# Revit family: PRE050012-FR
name_source: partatom
category: Accessoire de canalisation
revit_build: Autodesk Revit 2017 (Build: 20160225_1515(x64)
units: mm (PartAtom-declared; Revit-internal decimal feet)

## family parameters
Basée sur le plan de construction = Non
Cote de connecteur circulaire = Utiliser le diamètre
Couper avec des vides une fois chargée = Non
Partagée = Non
Toujours verticalement = Oui
Type d'élément = Normal

## types (5) — shared parameters
Adresse = 7, RUE RACINE - 92542 MONTROUGE CEDEX FRANCE
Diamètre Nominal = 12 mm  [stored 0.0393701 ft]
Fabricant = LES ROBINETS PRESTO S.A.
Finition = Composants en métal injecté avec traitement nickel-chrome

Corps en métal moulé injecté
Garantie = 3
Hauteur = 150 mm  [stored 0.492126 ft]
LC = 28 mm  [stored 0.0918635 ft]
Largeur = 56 mm  [stored 0.183727 ft]
Lien CCTP = http://www.prestodatashare.com
Lien fiche produit = http://www.prestodatashare.com
Lien notice d'utilisation = http://www.prestodatashare.com
Matériau = Laiton poli chromé
PC = 30 mm  [stored 0.0984252 ft]
Perte de charge = 0.0 Pa
Pression = 1 à 5 bars
Profondeur = 168 mm  [stored 0.551181 ft]
Raccordement = G 3/8" (12x17) en eau froide, chaude ou pré-mitigée
URL = http://www.prestodatashare.com
URL Fabricant = http://www.prestodatashare.com
Variantes = 56632-56633-56634-55635-56654

## per-type parameters (varying)
| type | Debit | Description | Flux | Fonction | Polantis code | Reference |
| 56632 PRESTO TOUCH SIMPLE PILE SS RA | 3 l/min par limiteur de débit intégré

Aérateur anti-tartre haute qualité

Dispositif anti-coup de bélier | Robinet simple sensitif (CE) temporisé (1s à 5mn) sur plage, alimentation en  eau froide ou mitigée. De type Presto TOUCH® réf. 56633 ou techniquement équivalent. Avec fonction start /stop par effleurement et régulateur de débit intégré (3 l/min). Alimentation par pile lithium 6 V intégrée dans le robinet. Avec flexibles PEX et filtre panier. Purge automatique paramétrable. | 0.1 L/s | Pression d'utilisation recommandée :
- 1 à 5 bars

Débit :
- 3 l/min par limiteur de débit intégré
- Aérateur anti-tartre haute qualité
- Dispositif anti-coup de bélier

Durée d'écoulement :
- 6 secondes (Réglable de 1 s à 5 min) et fonction marche/arrêt
- Fréquence et durée d'écoulement forcé paramétrables

Alimentation hydraulique:
- G 3/8" (12x17) en eau froide, chaude ou pré-mitigée

Alimentation électrique :
- Modèle avec pile lithium 6 volts type CRP2

Matière et couleur de finition :
- Composants en métal injecté avec traitement nickel-chrome
- Corps en métal moulé injecté

Résistance thermique :
- Ce robinet résiste à une température de 75°C durant 30 minutes dans le cadre de chocs thermiques

Sécurité :
- Fermeture automatique de l'électrovanne en cas d'usure de la pile

Livré avec :
- 1 Flexible PEX avec écrou femelle 3/8'' (12x17) et clapet anti-retour NF
- 1 Joint filtre monté dans une douille laiton
- 1 Bride de fixation
- 1 Joint de bride
- 1 Ecrou de fixation
- 1 Notice de pose

Normes / Agréments :
- Traitement de surface Nickel-chrome selon NF EN12540
- Résistance au brouillard salin neutre (NSS) : 200 h selon NF ISO 9227 | PRE050012-FR | 56632 |
| 56654 PRESTO TOUCH SIMPLE PILE RA - DEBIT 2L/MIN | 1,9 l/min par limiteur de débit intégré
 (sprayer)
 Aérateur anti-tartre haute qualité

 Dispositif anti-coup de bélier | Robinet simple sensitif (CE) temporisé (1s à 5mn) sur plage, alimentation en  eau froide ou mitigée. De type Presto TOUCH® réf. 56654 ou techniquement équivalent. Avec fonction start /stop par effleurement et limiteur de débit intégré (1,9 l/mn). Alimentation par pile lithium 6 V intégrée dans le robinet. Avec flexibles PEX, robinet d’arrêt droit et filtre panier. Purge automatique paramétrable. | 0.0 L/s | Pression d'utilisation recommandée :
- 1 à 5 bars

Débit :
- 1,9 l/min par sprayer limiteur de débit intégré
- Aérateur anti-tartre haute qualité
- Dispositif anti-coup de bélier

Durée d'écoulement :
- 6 secondes (Réglable de 1 s à 5 min) et fonction marche/arrêt
- Fréquence et durée d'écoulement forcé paramétrables

Alimentation hydraulique:
- G 3/8" (12x17) en eau froide, chaude ou pré-mitigée

Alimentation électrique :
- Modèle avec pile lithium 6 volts type CRP2

Matière et couleur de finition :
- Composants en métal injecté avec traitement nickel-chrome
- Corps en métal moulé injecté

Résistance thermique :
- Ce robinet résiste à une température de 75°C durant 30 minutes dans le cadre de chocs thermiques

Sécurité :
- Fermeture automatique de l'électrovanne en cas d'usure de la pile

Livré avec :
- 1 Flexible PEX avec écrou femelle 3/8'' (12x17) et clapet anti-retour NF
- 1 Joint filtre monté dans une douille laiton
- 1 Robinet d'arrêt droit G 3/8'' (12x17)
- 1 Bride de fixation
- 1 Joint de bride
- 1 Ecrou de fixation
- 1 Notice de pose

Normes / Agréments :
- Traitement de surface Nickel-chrome selon NF EN12540
- Résistance au brouillard salin neutre (NSS) : 200 h selon NF ISO 9227 | PRE050012d-FR | 56654 |
| 56635 PRESTO TOUCH SIMPLE SECTEUR RA | 3 l/min par limiteur de débit intégré

Aérateur anti-tartre haute qualité

Dispositif anti-coup de bélier | Robinet simple sensitif (CE) temporisé (1s à 5mn) sur plage, alimentation en  eau froide ou mitigée. De type Presto TOUCH® réf. 56635 ou techniquement équivalent. Avec fonction start /stop par effleurement et régulateur de débit intégré (3 l/min). Alimentation secteur par transformateur 230/7 Volt déporté dans boîtier étanche IP65. Avec flexible PEX, robinet d’arrêt droit et filtre panier. Purge automatique paramétrable. | 0.1 L/s | Pression d'utilisation recommandée :
- 1 à 5 bars

Débit :
- 3 l/min par limiteur de débit intégré
- Aérateur anti-tartre haute qualité
- Dispositif anti-coup de bélier

Durée d'écoulement :
- 6 secondes (Réglable de 1 s à 5 min) et fonction marche/arrêt
- Fréquence et durée d'écoulement forcé paramétrables

Alimentation hydraulique:
- G 3/8" (12x17) en eau froide, chaude ou pré-mitigée

Alimentation électrique :
- Avec transformateur 230 VAC / 7 VDC dans boîtier étanche IP65

Matière et couleur de finition :
- Composants en métal injecté avec traitement nickel-chrome
- Corps en métal moulé injecté

Résistance thermique :
- Ce robinet résiste à une température de 75°C durant 30 minutes dans le cadre de chocs thermiques

Sécurité :
- Fermeture automatique de l'électrovanne en cas d'absence d'alimentation

Livré avec :
- 1 Flexible PEX avec écrou femelle 3/8" (12x17) et clapet anti-retour NF
- 1 Joint filtre monté dans une douille laiton
- 1 Robinet d'arrêt droit G 3/8'' (12x17)
- 1 Bride de fixation
- 1 Joint de bride
- 1 Ecrou de fixation
- 1 Notice de pose

Normes / Agréments :
- Traitement de surface Nickel-chrome selon NF EN12540
- Résistance au brouillard salin neutre (NSS) : 200 h selon NF ISO 9227 | PRE050012c-FR | 56635 |
| 56634 PRESTO TOUCH SIMPLE SECTEUR SS RA | 3 l/min par limiteur de débit intégré

Aérateur anti-tartre haute qualité

Dispositif anti-coup de bélier | Robinet simple sensitif (CE) temporisé (1s à 5mn) sur plage, alimentation en  eau froide ou mitigée. De type Presto TOUCH® réf. 56634 ou techniquement équivalent. Avec fonction start /stop par effleurement et régulateur de débit intégré (3 l/min). Alimentation secteur par transformateur 230/7 Volt déporté dans boîtier étanche IP65. Avec flexible PEX  et filtre panier. Purge automatique paramétrable. | 0.1 L/s | Pression d'utilisation recommandée :
- 1 à 5 bars

Débit :
- 3 l/min par limiteur de débit intégré
- Aérateur anti-tartre haute qualité
- Dispositif anti-coup de bélier

Durée d'écoulement :
- 6 secondes (Réglable de 1 s à 5 min) et fonction marche/arrêt
- Fréquence et durée d'écoulement forcé paramétrables

Alimentation hydraulique:
- G 3/8" (12x17) en eau froide, chaude ou pré-mitigée

Alimentation électrique :
- Avec transformateur 230 VAC / 7 VDC dans boîtier étanche IP65

Matière et couleur de finition :
- Composants en métal injecté avec traitement nickel-chrome
- Corps en métal moulé injecté

Résistance thermique :
- Ce robinet résiste à une température de 75°C durant 30 minutes dans le cadre de chocs thermiques

Sécurité :
- Fermeture automatique de l'électrovanne en cas d'absence d'alimentation

Livré avec :
- 1 Flexible PEX avec écrou femelle 3/8" (12x17) et clapet anti-retour NF
- 1 Joint filtre monté dans une douille laiton
- 1 Bride de fixation
- 1 Joint de bride
- 1 Ecrou de fixation
- 1 Notice de pose

Normes / Agréments :
- Traitement de surface Nickel-chrome selon NF EN12540
- Résistance au brouillard salin neutre (NSS) : 200 h selon NF ISO 9227 | PRE050012b-FR | 56634 |
| 56633 PRESTO TOUCH SIMPLE PILE RA | 3 l/min par limiteur de débit intégré

Aérateur anti-tartre haute qualité

Dispositif anti-coup de bélier | Robinet simple sensitif (CE) temporisé (1s à 5mn) sur plage, alimentation en  eau froide ou mitigée. De type Presto TOUCH® réf. 56633 ou techniquement équivalent. Avec fonction start /stop par effleurement et régulateur de débit intégré (3 l/min). Alimentation par pile lithium 6 V intégrée dans le robinet. Avec flexibles PEX, robinet d’arrêt droit et filtre panier. Purge automatique paramétrable. | 0.1 L/s | Pression d'utilisation recommandée :
- 1 à 5 bars

Débit :
- 3 l/min par limiteur de débit intégré
- Aérateur anti-tartre haute qualité
- Dispositif anti-coup de bélier

Durée d'écoulement :
- 6 secondes (Réglable de 1 s à 5 min) et fonction marche/arrêt
- Fréquence et durée d'écoulement forcé paramétrables

Alimentation hydraulique:
- G 3/8" (12x17) en eau froide, chaude ou pré-mitigée

Alimentation électrique :
- Modèle avec pile lithium 6 volts type CRP2

Matière et couleur de finition :
- Composants en métal injecté avec traitement nickel-chrome
- Corps en métal moulé injecté

Résistance thermique :
- Ce robinet résiste à une température de 75°C durant 30 minutes dans le cadre de chocs thermiques

Sécurité :
- Fermeture automatique de l'électrovanne en cas d'usure de la pile

Livré avec :
- 1 Flexible PEX avec écrou femelle 3/8'' (12x17) et clapet anti-retour NF
- 1 Joint filtre monté dans une douille laiton
- 1 Robinet d'arrêt droit G 3/8'' (12x17)
- 1 Bride de fixation
- 1 Joint de bride
- 1 Ecrou de fixation
- 1 Notice de pose

Normes / Agréments :
- Traitement de surface Nickel-chrome selon NF EN12540
- Résistance au brouillard salin neutre (NSS) : 200 h selon NF ISO 9227 | PRE050012a-FR | 56633 |

note: column(s) folded — value = type name in every type: Modèle

note: [stored X ft] marks values corroborated as IEEE doubles in the binary element streams (Revit-internal decimal feet)
